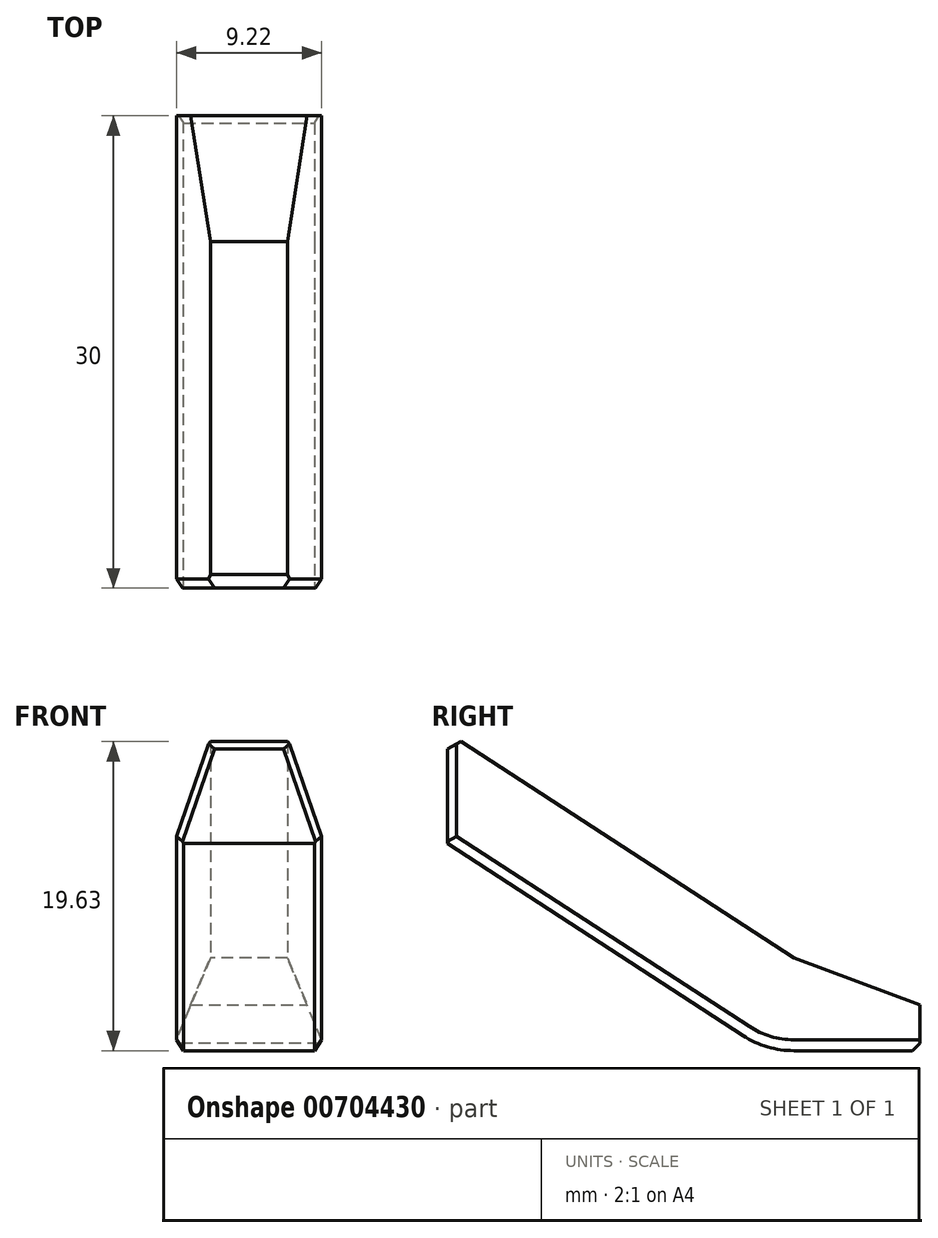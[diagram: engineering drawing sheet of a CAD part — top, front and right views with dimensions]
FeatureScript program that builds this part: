
annotation { "Feature Type Name" : "Feature", "Feature Type Description" : "" }
export const myFeature = defineFeature(function(context is Context, id is Id, definition is map)
    precondition{}
    {
        {
            var Q0;
            Q0=qCreatedBy(makeId("Front.planeOp"),FACE);
            var sketch = newSketch(context, id + "F0", { "sketchPlane" : qUnion([Q0])});
            skLineSegment(sketch, "E0", {"start": v(-4.9, 0) * mm, "end": v(4.9, 0) * mm});
            skLineSegment(sketch, "E1", {"start": v(4.9, 0) * mm, "end": v(2.45, 5.9) * mm});
            skLineSegment(sketch, "E2", {"start": v(2.45, 5.9) * mm, "end": v(-2.45, 5.9) * mm});
            skLineSegment(sketch, "E3", {"start": v(-2.45, 5.9) * mm, "end": v(-4.9, 0) * mm});
            skSolve(sketch);
        }
        {
            var Q0;
            Q0 = qSketchRegion(id + "F0", true);
            extrude(context, id + "F1", {"entities" : qUnion([Q0]), "depth" : 8 * mm, "offsetDistance" : 25 * mm});
        }
        {
            var Q0;
            Q0=makeQuery(id+"F1.opExtrude","CAP_FACE",FACE,{"disambiguationData":[OSD([sQuery(id+"F0.wireOp",EDGE,"E0"),sQuery(id+"F0.wireOp",EDGE,"E1"),sQuery(id+"F0.wireOp",EDGE,"E2"),sQuery(id+"F0.wireOp",EDGE,"E3")])],"isStart":false});
            var sketch = newSketch(context, id + "F2", { "sketchPlane" : qUnion([Q0])});
            skLineSegment(sketch, "E4.0.0", {"start": v(2.45, 5.9) * mm, "end": v(-2.45, 5.9) * mm});
            skLineSegment(sketch, "E4.0.1", {"start": v(-2.45, 5.9) * mm, "end": v(-4.9, 0) * mm});
            skLineSegment(sketch, "E4.0.2", {"start": v(-4.9, 0) * mm, "end": v(4.9, 0) * mm});
            skLineSegment(sketch, "E4.0.3", {"start": v(4.9, 0) * mm, "end": v(2.45, 5.9) * mm});
            skSolve(sketch);
        }
        {
            var Q0;
            Q0 = qSketchRegion(id + "F2", true);
            var Q1;
            Q1=sQuery(id+"F2.wireOp",EDGE,"E4.0.0");
            revolve(context, id + "F3", {"operationType" : NewBodyOperationType.ADD, "surfaceOperationType" : NewSurfaceOperationType.NEW, "entities" : qUnion([Q0]), "axis" : qUnion([Q1]), "revolveType" : RevolveType.ONE_DIRECTION, "angle" : 33 * degree});
        }
        {
            var Q0;
            Q0=makeQuery(id+"F3.opRevolve","CAP_FACE",FACE,{"disambiguationData":[OSD([sQuery(id+"F2.wireOp",EDGE,"E4.0.0"),sQuery(id+"F2.wireOp",EDGE,"E4.0.1"),sQuery(id+"F2.wireOp",EDGE,"E4.0.2"),sQuery(id+"F2.wireOp",EDGE,"E4.0.3")])],"isStart":false});
            var sketch = newSketch(context, id + "F4", { "sketchPlane" : qUnion([Q0])});
            skLineSegment(sketch, "E5.0.0", {"start": v(4.9, -5.3) * mm, "end": v(2.45, 0.6) * mm});
            skLineSegment(sketch, "E5.0.1", {"start": v(2.45, 0.6) * mm, "end": v(-2.45, 0.6) * mm});
            skLineSegment(sketch, "E5.0.2", {"start": v(-2.45, 0.6) * mm, "end": v(-4.9, -5.3) * mm});
            skLineSegment(sketch, "E5.0.3", {"start": v(-4.9, -5.3) * mm, "end": v(4.9, -5.3) * mm});
            skSolve(sketch);
        }
        {
            var Q0;
            Q0=makeQuery(id+"F1.opExtrude","CAP_FACE",FACE,{"disambiguationData":[OSD([sQuery(id+"F0.wireOp",EDGE,"E0"),sQuery(id+"F0.wireOp",EDGE,"E1"),sQuery(id+"F0.wireOp",EDGE,"E2"),sQuery(id+"F0.wireOp",EDGE,"E3")])],"isStart":true});
            cPlane(context, id + "F5", {"entities" : qUnion([Q0]), "cplaneType" : CPlaneType.OFFSET, "offset" : 30 * mm, "oppositeDirection" : true, "width" : 150 * mm, "height" : 150 * mm});
        }
        {
            var Q0;
            Q0 = qSketchRegion(id + "F4", true);
            extrude(context, id + "F6", {"entities" : qUnion([Q0]), "operationType" : NewBodyOperationType.ADD, "depth" : 26.5 * mm, "offsetDistance" : 25 * mm});
        }
        {
            var Q0;
            Q0=qCreatedBy(makeId("Top.planeOp"),FACE);
            var sketch = newSketch(context, id + "F7", { "sketchPlane" : qUnion([Q0])});
            skLineSegment(sketch, "E6.bottom", {"start": v(-8.41, -39.64) * mm, "end": v(10.08, -39.64) * mm});
            skLineSegment(sketch, "E6.top", {"start": v(-8.41, -30) * mm, "end": v(10.08, -30) * mm});
            skLineSegment(sketch, "E6.left", {"start": v(-8.41, -39.64) * mm, "end": v(-8.41, -30) * mm});
            skLineSegment(sketch, "E6.right", {"start": v(10.08, -39.64) * mm, "end": v(10.08, -30) * mm});
            skSolve(sketch);
        }
        {
            var Q0;
            Q0 = qSketchRegion(id + "F7", true);
            extrude(context, id + "F8", {"entities" : qUnion([Q0]), "operationType" : NewBodyOperationType.REMOVE, "depth" : 25 * mm, "offsetDistance" : 25 * mm});
        }
        {
            var Q0;
            Q0=makeQuery(id+"F1.opExtrude","SWEPT_EDGE",EDGE,{"disambiguationData":[OSD([sQuery(id+"F0.wireOp",EDGE,"E0"),sQuery(id+"F0.wireOp",EDGE,"E1")])]});
            var Q1;
            Q1=makeQuery(id+"F1.opExtrude","SWEPT_EDGE",EDGE,{"disambiguationData":[OSD([sQuery(id+"F0.wireOp",EDGE,"E0"),sQuery(id+"F0.wireOp",EDGE,"E3")])]});
            chamfer(context, id + "F9", {"entities" : qUnion([Q0, Q1]), "width" : 0.5 * mm, "tangentPropagation" : true});
        }
        {
            var Q0;
            Q0=makeQuery(id+"F1.opExtrude","CAP_EDGE",EDGE,{"disambiguationData":[OSD([sQuery(id+"F0.wireOp",EDGE,"E2")])],"isStart":true});
            chamfer(context, id + "F10", {"entities" : qUnion([Q0]), "chamferType" : ChamferType.TWO_OFFSETS, "width1" : 8 * mm, "oppositeDirection" : false, "width2" : 3 * mm, "tangentPropagation" : true});
        }
        {
            var Q0;
            Q0=makeQuery(id+"F1.opExtrude","CAP_EDGE",EDGE,{"disambiguationData":[OSD([sQuery(id+"F0.wireOp",EDGE,"E0")])],"isStart":true});
            chamfer(context, id + "F11", {"entities" : qUnion([Q0]), "width" : 0.46 * mm, "tangentPropagation" : true});
        }
        {
            var Q0;
            Q0=makeQuery(id+"F8.boolean.opBoolean","INTERSECT",EDGE,{"derivedFrom":[makeQuery(id+"F6.opExtrude","SWEPT_FACE",FACE,{"disambiguationData":[OSD([sQuery(id+"F4.wireOp",EDGE,"E5.0.2")])]}),makeQuery(id+"F8.opExtrude","SWEPT_FACE",FACE,{"disambiguationData":[OSD([sQuery(id+"F7.wireOp",EDGE,"E6.top")])]})]});
            var Q1;
            Q1=makeQuery(id+"F8.boolean.opBoolean","INTERSECT",EDGE,{"derivedFrom":[makeQuery(id+"F6.opExtrude","SWEPT_FACE",FACE,{"disambiguationData":[OSD([sQuery(id+"F4.wireOp",EDGE,"E5.0.0")])]}),makeQuery(id+"F8.opExtrude","SWEPT_FACE",FACE,{"disambiguationData":[OSD([sQuery(id+"F7.wireOp",EDGE,"E6.top")])]})]});
            chamfer(context, id + "F12", {"entities" : qUnion([Q0, Q1]), "width" : 0.47 * mm, "tangentPropagation" : true});
        }
        {
            var Q0;
            Q0=makeQuery(id+"F8.boolean.opBoolean","INTERSECT",EDGE,{"derivedFrom":[makeQuery(id+"F6.opExtrude","SWEPT_FACE",FACE,{"disambiguationData":[OSD([sQuery(id+"F4.wireOp",EDGE,"E5.0.1")])]}),makeQuery(id+"F8.opExtrude","SWEPT_FACE",FACE,{"disambiguationData":[OSD([sQuery(id+"F7.wireOp",EDGE,"E6.top")])]})]});
            chamfer(context, id + "F13", {"entities" : qUnion([Q0]), "width" : 0.56 * mm, "tangentPropagation" : true});
        }
        {
            var Q0;
            {var subQ0=sQuery(id+"F0.wireOp",EDGE,"E0");Q0=makeQuery(id+"F9.opChamfer","BLEND_EDGE",EDGE,{"blendedFrom":[makeQuery(id+"F1.opExtrude","SWEPT_EDGE",EDGE,{"disambiguationData":[OSD([subQ0,sQuery(id+"F0.wireOp",EDGE,"E1")])]}),makeQuery(id+"F1.opExtrude","SWEPT_FACE",FACE,{"disambiguationData":[OSD([subQ0])]})],"blendedInto":[makeQuery(id+"F1.opExtrude","SWEPT_FACE",FACE,{"disambiguationData":[OSD([subQ0])]})]});}
            cPlane(context, id + "F14", {"entities" : qUnion([Q0]), "cplaneType" : CPlaneType.LINE_ANGLE, "offset" : 25 * mm, "angle" : 90 * degree, "width" : 150 * mm, "height" : 150 * mm});
        }
    });
